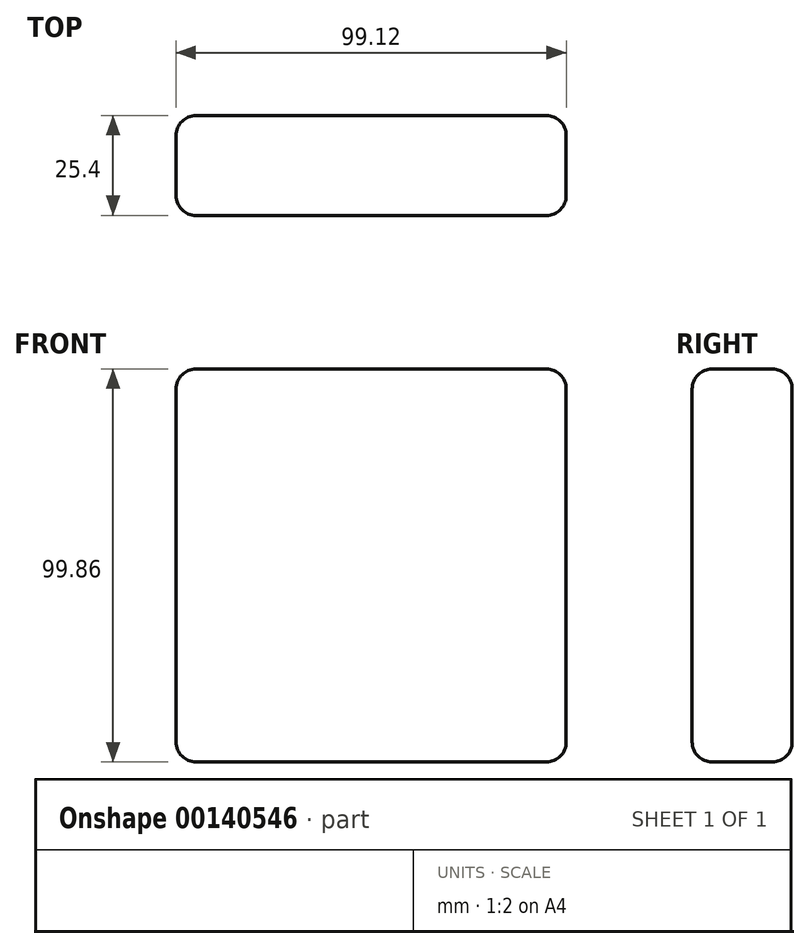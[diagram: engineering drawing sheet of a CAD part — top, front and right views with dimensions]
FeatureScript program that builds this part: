
annotation { "Feature Type Name" : "Feature", "Feature Type Description" : "" }
export const myFeature = defineFeature(function(context is Context, id is Id, definition is map)
    precondition{}
    {
        {
            var Q0;
            Q0=qCreatedBy(makeId("Front.planeOp"),FACE);
            var sketch = newSketch(context, id + "F0", { "sketchPlane" : qUnion([Q0])});
            skLineSegment(sketch, "E0.bottom", {"start": v(-75.38, 76.38) * mm, "end": v(23.74, 76.38) * mm});
            skLineSegment(sketch, "E0.top", {"start": v(-75.38, -23.48) * mm, "end": v(23.74, -23.48) * mm});
            skLineSegment(sketch, "E0.left", {"start": v(-75.38, 76.38) * mm, "end": v(-75.38, -23.48) * mm});
            skLineSegment(sketch, "E0.right", {"start": v(23.74, 76.38) * mm, "end": v(23.74, -23.48) * mm});
            skSolve(sketch);
        }
        {
            var Q0;
            Q0=makeQuery(id+"F0.imprint","IMPRINT",FACE,{"disambiguationData":[TD([[makeQuery(id+"F0.imprint","IMPRINT",EDGE,{"derivedFrom":sQuery(id+"F0.wireOp",EDGE,"E0.bottom")}),-1.0]])]});
            extrude(context, id + "F1", {"entities" : qUnion([Q0]), "depth" : 25.4 * mm});
        }
        {
            var Q0;
            Q0=makeQuery(id+"F1.opExtrude","CAP_EDGE",EDGE,{"disambiguationData":[OSD([sQuery(id+"F0.wireOp",EDGE,"E0.right")])],"isStart":false});
            var Q1;
            Q1=makeQuery(id+"F1.opExtrude","CAP_EDGE",EDGE,{"disambiguationData":[OSD([sQuery(id+"F0.wireOp",EDGE,"E0.right")])],"isStart":true});
            fillet(context, id + "F2", {"entities" : qUnion([Q0, Q1]), "radius" : 5.08 * mm, "tangentPropagation" : true, "allowEdgeOverflow" : false});
        }
        {
            var Q0;
            Q0=makeQuery(id+"F1.opExtrude","CAP_EDGE",EDGE,{"disambiguationData":[OSD([sQuery(id+"F0.wireOp",EDGE,"E0.top")])],"isStart":false});
            var Q1;
            Q1=makeQuery(id+"F1.opExtrude","CAP_EDGE",EDGE,{"disambiguationData":[OSD([sQuery(id+"F0.wireOp",EDGE,"E0.top")])],"isStart":true});
            var Q2;
            Q2=makeQuery(id+"F1.opExtrude","CAP_FACE",FACE,{"disambiguationData":[OSD([sQuery(id+"F0.wireOp",EDGE,"E0.bottom"),sQuery(id+"F0.wireOp",EDGE,"E0.top"),sQuery(id+"F0.wireOp",EDGE,"E0.left"),sQuery(id+"F0.wireOp",EDGE,"E0.right")])],"isStart":false});
            var Q3;
            Q3=makeQuery(id+"F1.opExtrude","SWEPT_FACE",FACE,{"disambiguationData":[OSD([sQuery(id+"F0.wireOp",EDGE,"E0.left")])]});
            var Q4;
            {var subQ0=sQuery(id+"F0.wireOp",EDGE,"E0.right");Q4=makeQuery(id+"F2.opFillet","BLEND_FACE",FACE,{"disambiguationData":[OSD([subQ0]),TDD([makeQuery(id+"F1.opExtrude","CAP_EDGE",EDGE,{"disambiguationData":[OSD([subQ0])],"isStart":true})])]});}
            var Q5;
            Q5=makeQuery(id+"F1.opExtrude","SWEPT_EDGE",EDGE,{"disambiguationData":[OSD([sQuery(id+"F0.wireOp",EDGE,"E0.top"),sQuery(id+"F0.wireOp",EDGE,"E0.left")])]});
            var Q6;
            {var subQ0=sQuery(id+"F0.wireOp",EDGE,"E0.right");Q6=makeQuery(id+"F2.opFillet","BLEND_FACE",FACE,{"disambiguationData":[OSD([subQ0]),TDD([makeQuery(id+"F1.opExtrude","CAP_EDGE",EDGE,{"disambiguationData":[OSD([subQ0])],"isStart":false})])]});}
            var Q7;
            Q7=makeQuery(id+"F1.opExtrude","SWEPT_EDGE",EDGE,{"disambiguationData":[OSD([sQuery(id+"F0.wireOp",EDGE,"E0.bottom"),sQuery(id+"F0.wireOp",EDGE,"E0.left")])]});
            var Q8;
            Q8=makeQuery(id+"F1.opExtrude","CAP_EDGE",EDGE,{"disambiguationData":[OSD([sQuery(id+"F0.wireOp",EDGE,"E0.bottom")])],"isStart":false});
            var Q9;
            Q9=makeQuery(id+"F1.opExtrude","CAP_EDGE",EDGE,{"disambiguationData":[OSD([sQuery(id+"F0.wireOp",EDGE,"E0.bottom")])],"isStart":true});
            var Q10;
            Q10=makeQuery(id+"F1.opExtrude","CAP_EDGE",EDGE,{"disambiguationData":[OSD([sQuery(id+"F0.wireOp",EDGE,"E0.left")])],"isStart":true});
            var Q11;
            {var subQ0=sQuery(id+"F0.wireOp",EDGE,"E0.right");Q11=makeQuery(id+"F2.opFillet","BLEND_EDGE",EDGE,{"blendedFrom":[makeQuery(id+"F1.opExtrude","CAP_EDGE",EDGE,{"disambiguationData":[OSD([subQ0])],"isStart":false}),makeQuery(id+"F1.opExtrude","CAP_FACE",FACE,{"disambiguationData":[OSD([sQuery(id+"F0.wireOp",EDGE,"E0.bottom"),sQuery(id+"F0.wireOp",EDGE,"E0.top"),sQuery(id+"F0.wireOp",EDGE,"E0.left"),subQ0])],"isStart":false})],"blendedInto":[makeQuery(id+"F1.opExtrude","CAP_FACE",FACE,{"disambiguationData":[OSD([sQuery(id+"F0.wireOp",EDGE,"E0.bottom"),sQuery(id+"F0.wireOp",EDGE,"E0.top"),sQuery(id+"F0.wireOp",EDGE,"E0.left"),subQ0])],"isStart":false})]});}
            var Q12;
            Q12=makeQuery(id+"F1.opExtrude","SWEPT_FACE",FACE,{"disambiguationData":[OSD([sQuery(id+"F0.wireOp",EDGE,"E0.bottom")])]});
            var Q13;
            Q13=makeQuery(id+"F1.opExtrude","CAP_FACE",FACE,{"disambiguationData":[OSD([sQuery(id+"F0.wireOp",EDGE,"E0.bottom"),sQuery(id+"F0.wireOp",EDGE,"E0.top"),sQuery(id+"F0.wireOp",EDGE,"E0.left"),sQuery(id+"F0.wireOp",EDGE,"E0.right")])],"isStart":true});
            var Q14;
            Q14=makeQuery(id+"F1.opExtrude","SWEPT_EDGE",EDGE,{"disambiguationData":[OSD([sQuery(id+"F0.wireOp",EDGE,"E0.bottom"),sQuery(id+"F0.wireOp",EDGE,"E0.right")])]});
            var Q15;
            Q15=makeQuery(id+"F1.opExtrude","SWEPT_EDGE",EDGE,{"disambiguationData":[OSD([sQuery(id+"F0.wireOp",EDGE,"E0.top"),sQuery(id+"F0.wireOp",EDGE,"E0.right")])]});
            var Q16;
            Q16=makeQuery(id+"F2.opFillet","BLEND_EDGE",EDGE,{"blendedFrom":[makeQuery(id+"F1.opExtrude","CAP_EDGE",EDGE,{"disambiguationData":[OSD([sQuery(id+"F0.wireOp",EDGE,"E0.right")])],"isStart":true}),makeQuery(id+"F1.opExtrude","SWEPT_FACE",FACE,{"disambiguationData":[OSD([sQuery(id+"F0.wireOp",EDGE,"E0.bottom")])]})],"blendedInto":[makeQuery(id+"F1.opExtrude","SWEPT_FACE",FACE,{"disambiguationData":[OSD([sQuery(id+"F0.wireOp",EDGE,"E0.bottom")])]})]});
            var Q17;
            {var subQ0=sQuery(id+"F0.wireOp",EDGE,"E0.right");Q17=makeQuery(id+"F2.opFillet","BLEND_EDGE",EDGE,{"blendedFrom":[makeQuery(id+"F1.opExtrude","CAP_EDGE",EDGE,{"disambiguationData":[OSD([subQ0])],"isStart":false}),makeQuery(id+"F1.opExtrude","SWEPT_FACE",FACE,{"disambiguationData":[OSD([subQ0])]})],"blendedInto":[makeQuery(id+"F1.opExtrude","SWEPT_FACE",FACE,{"disambiguationData":[OSD([subQ0])]})]});}
            var Q18;
            Q18=makeQuery(id+"F1.opExtrude","CAP_EDGE",EDGE,{"disambiguationData":[OSD([sQuery(id+"F0.wireOp",EDGE,"E0.left")])],"isStart":false});
            var Q19;
            Q19=makeQuery(id+"F1.opExtrude","SWEPT_FACE",FACE,{"disambiguationData":[OSD([sQuery(id+"F0.wireOp",EDGE,"E0.right")])]});
            var Q20;
            {var subQ0=sQuery(id+"F0.wireOp",EDGE,"E0.right");Q20=makeQuery(id+"F2.opFillet","BLEND_EDGE",EDGE,{"blendedFrom":[makeQuery(id+"F1.opExtrude","CAP_EDGE",EDGE,{"disambiguationData":[OSD([subQ0])],"isStart":true}),makeQuery(id+"F1.opExtrude","CAP_FACE",FACE,{"disambiguationData":[OSD([sQuery(id+"F0.wireOp",EDGE,"E0.bottom"),sQuery(id+"F0.wireOp",EDGE,"E0.top"),sQuery(id+"F0.wireOp",EDGE,"E0.left"),subQ0])],"isStart":true})],"blendedInto":[makeQuery(id+"F1.opExtrude","CAP_FACE",FACE,{"disambiguationData":[OSD([sQuery(id+"F0.wireOp",EDGE,"E0.bottom"),sQuery(id+"F0.wireOp",EDGE,"E0.top"),sQuery(id+"F0.wireOp",EDGE,"E0.left"),subQ0])],"isStart":true})]});}
            var Q21;
            {var subQ0=sQuery(id+"F0.wireOp",EDGE,"E0.right");Q21=makeQuery(id+"F2.opFillet","BLEND_EDGE",EDGE,{"blendedFrom":[makeQuery(id+"F1.opExtrude","CAP_EDGE",EDGE,{"disambiguationData":[OSD([subQ0])],"isStart":true}),makeQuery(id+"F1.opExtrude","SWEPT_FACE",FACE,{"disambiguationData":[OSD([subQ0])]})],"blendedInto":[makeQuery(id+"F1.opExtrude","SWEPT_FACE",FACE,{"disambiguationData":[OSD([subQ0])]})]});}
            var Q22;
            Q22=makeQuery(id+"F1.opExtrude","SWEPT_FACE",FACE,{"disambiguationData":[OSD([sQuery(id+"F0.wireOp",EDGE,"E0.top")])]});
            var Q23;
            Q23=makeQuery(id+"F2.opFillet","BLEND_EDGE",EDGE,{"blendedFrom":[makeQuery(id+"F1.opExtrude","CAP_EDGE",EDGE,{"disambiguationData":[OSD([sQuery(id+"F0.wireOp",EDGE,"E0.right")])],"isStart":false}),makeQuery(id+"F1.opExtrude","SWEPT_FACE",FACE,{"disambiguationData":[OSD([sQuery(id+"F0.wireOp",EDGE,"E0.bottom")])]})],"blendedInto":[makeQuery(id+"F1.opExtrude","SWEPT_FACE",FACE,{"disambiguationData":[OSD([sQuery(id+"F0.wireOp",EDGE,"E0.bottom")])]})]});
            var Q24;
            Q24=makeQuery(id+"F2.opFillet","BLEND_EDGE",EDGE,{"blendedFrom":[makeQuery(id+"F1.opExtrude","CAP_EDGE",EDGE,{"disambiguationData":[OSD([sQuery(id+"F0.wireOp",EDGE,"E0.right")])],"isStart":false}),makeQuery(id+"F1.opExtrude","SWEPT_FACE",FACE,{"disambiguationData":[OSD([sQuery(id+"F0.wireOp",EDGE,"E0.top")])]})],"blendedInto":[makeQuery(id+"F1.opExtrude","SWEPT_FACE",FACE,{"disambiguationData":[OSD([sQuery(id+"F0.wireOp",EDGE,"E0.top")])]})]});
            var Q25;
            Q25=makeQuery(id+"F2.opFillet","BLEND_EDGE",EDGE,{"blendedFrom":[makeQuery(id+"F1.opExtrude","CAP_EDGE",EDGE,{"disambiguationData":[OSD([sQuery(id+"F0.wireOp",EDGE,"E0.right")])],"isStart":true}),makeQuery(id+"F1.opExtrude","SWEPT_FACE",FACE,{"disambiguationData":[OSD([sQuery(id+"F0.wireOp",EDGE,"E0.top")])]})],"blendedInto":[makeQuery(id+"F1.opExtrude","SWEPT_FACE",FACE,{"disambiguationData":[OSD([sQuery(id+"F0.wireOp",EDGE,"E0.top")])]})]});
            fillet(context, id + "F3", {"entities" : qUnion([Q0, Q1, Q2, Q3, Q4, Q5, Q6, Q7, Q8, Q9, Q10, Q11, Q12, Q13, Q14, Q15, Q16, Q17, Q18, Q19, Q20, Q21, Q22, Q23, Q24, Q25]), "radius" : 5.08 * mm, "tangentPropagation" : true, "allowEdgeOverflow" : false});
        }
    });
